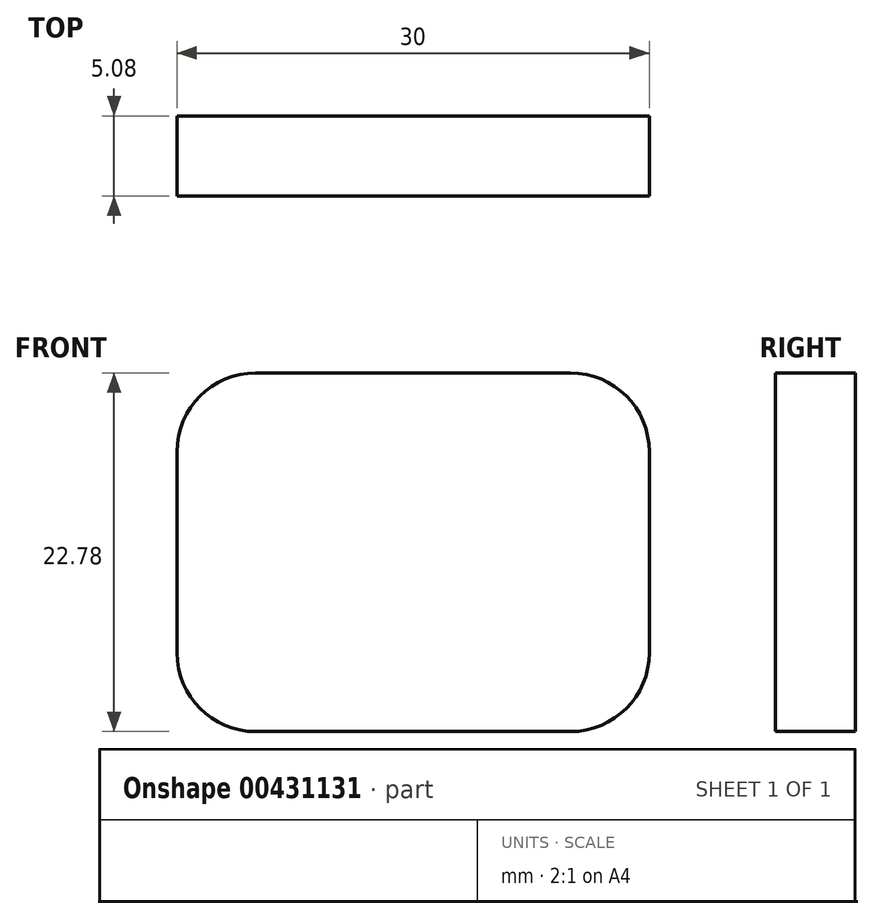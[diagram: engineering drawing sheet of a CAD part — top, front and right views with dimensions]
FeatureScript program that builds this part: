
annotation { "Feature Type Name" : "Feature", "Feature Type Description" : "" }
export const myFeature = defineFeature(function(context is Context, id is Id, definition is map)
    precondition{}
    {
        {
            var Q0;
            Q0=qCreatedBy(makeId("Front.planeOp"),FACE);
            var sketch = newSketch(context, id + "F0", { "sketchPlane" : qUnion([Q0])});
            skLineSegment(sketch, "E0.bottom", {"start": v(-10, 11.39) * mm, "end": v(10, 11.39) * mm});
            skLineSegment(sketch, "E0.top", {"start": v(-10, -11.39) * mm, "end": v(10, -11.39) * mm});
            skLineSegment(sketch, "E0.left", {"start": v(-15, 6.39) * mm, "end": v(-15, -6.39) * mm});
            skLineSegment(sketch, "E0.right", {"start": v(15, 6.39) * mm, "end": v(15, -6.39) * mm});
            skPoint(sketch, "E0.middle", {"position": v(0, 0) * mm});
            skPoint(sketch, "E1.visualSharp", {"position": v(-15, 11.39) * mm});
            skArc(sketch, "E1.filletArc", {"start": v(-10, 11.39) * mm, "mid": v(-13.54, 9.92) * mm, "end": v(-15, 6.39) * mm});
            skPoint(sketch, "E2.visualSharp", {"position": v(15, 11.39) * mm});
            skArc(sketch, "E2.filletArc", {"start": v(15, 6.39) * mm, "mid": v(13.54, 9.92) * mm, "end": v(10, 11.39) * mm});
            skPoint(sketch, "E3.visualSharp", {"position": v(15, -11.39) * mm});
            skArc(sketch, "E3.filletArc", {"start": v(10, -11.39) * mm, "mid": v(13.54, -9.92) * mm, "end": v(15, -6.39) * mm});
            skPoint(sketch, "E4.visualSharp", {"position": v(-15, -11.39) * mm});
            skArc(sketch, "E4.filletArc", {"start": v(-15, -6.39) * mm, "mid": v(-13.54, -9.92) * mm, "end": v(-10, -11.39) * mm});
            skSolve(sketch);
        }
        {
            var Q0;
            Q0=makeQuery(id+"F0.imprint","IMPRINT",FACE,{"disambiguationData":[TD([[makeQuery(id+"F0.imprint","IMPRINT",EDGE,{"derivedFrom":sQuery(id+"F0.wireOp",EDGE,"E0.bottom")}),-1.0]])]});
            extrude(context, id + "F1", {"entities" : qUnion([Q0]), "depth" : 5.08 * mm});
        }
    });
